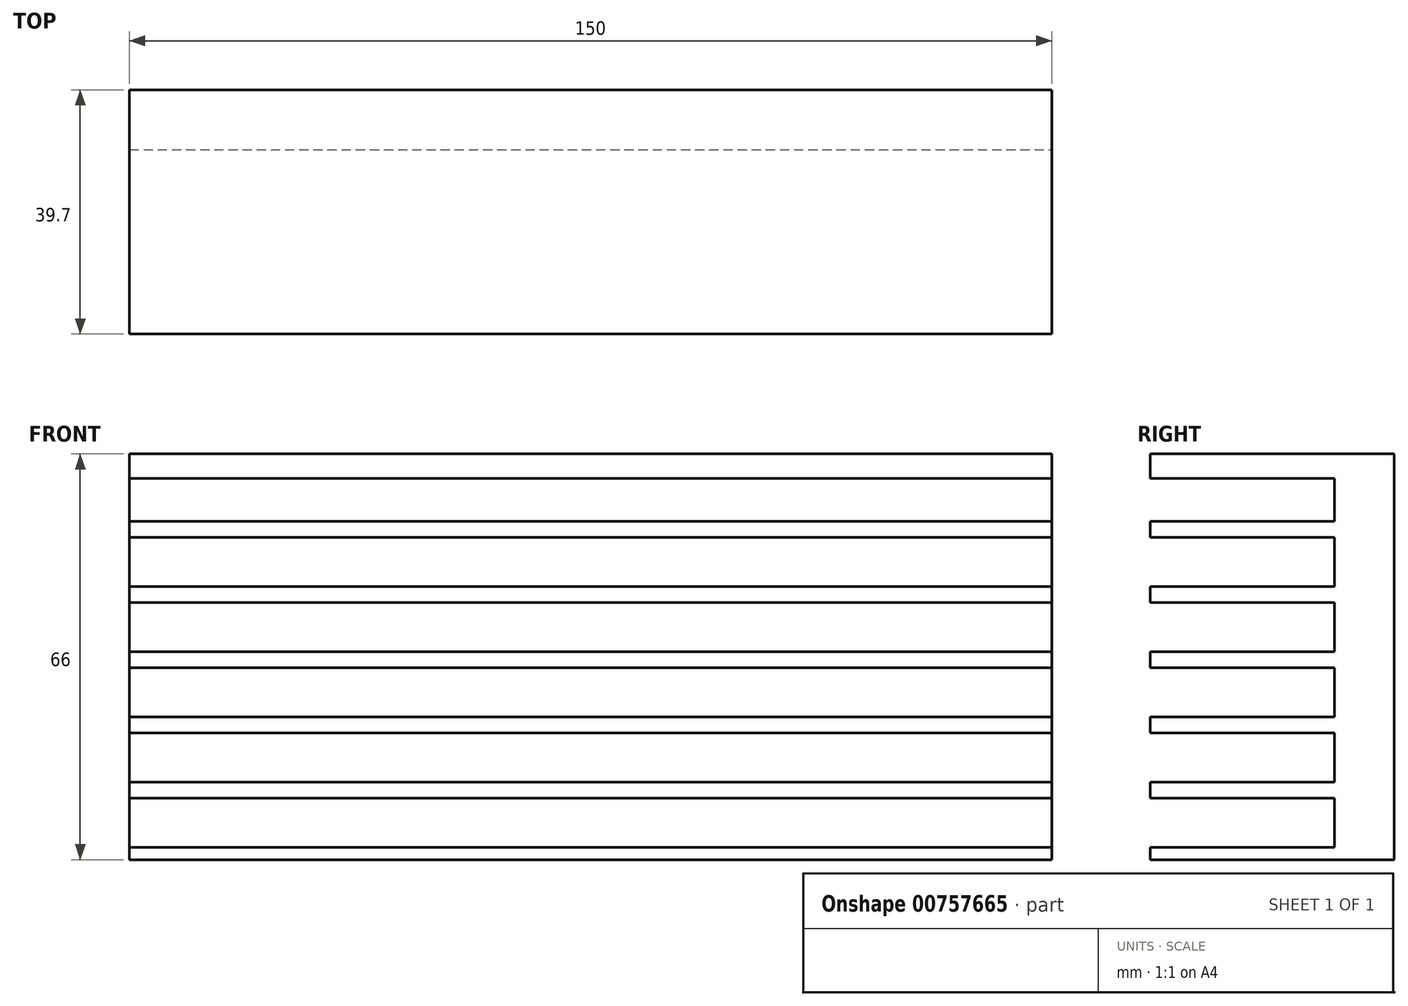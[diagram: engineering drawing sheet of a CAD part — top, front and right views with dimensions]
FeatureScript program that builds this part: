
annotation { "Feature Type Name" : "Feature", "Feature Type Description" : "" }
export const myFeature = defineFeature(function(context is Context, id is Id, definition is map)
    precondition{}
    {
        {
            var Q0;
            Q0=qCreatedBy(makeId("Front.planeOp"),FACE);
            var sketch = newSketch(context, id + "F0", { "sketchPlane" : qUnion([Q0])});
            skLineSegment(sketch, "E0.bottom", {"start": v(-143.7, 34.15) * mm, "end": v(6.3, 34.15) * mm});
            skLineSegment(sketch, "E0.top", {"start": v(-143.7, -31.85) * mm, "end": v(6.3, -31.85) * mm});
            skLineSegment(sketch, "E0.left", {"start": v(-143.7, 34.15) * mm, "end": v(-143.7, -31.85) * mm});
            skLineSegment(sketch, "E0.right", {"start": v(6.3, 34.15) * mm, "end": v(6.3, -31.85) * mm});
            skSolve(sketch);
        }
        {
            var Q0;
            Q0 = qSketchRegion(id + "F0", true);
            var Q1;
            Q1=makeQuery(id+"F0.imprint","IMPRINT",FACE,{"disambiguationData":[TD([[makeQuery(id+"F0.imprint","IMPRINT",EDGE,{"derivedFrom":sQuery(id+"F0.wireOp",EDGE,"E0.bottom")}),-1.0]])]});
            extrude(context, id + "F1", {"entities" : qUnion([Q0, Q1]), "depth" : 39.7 * mm, "offsetDistance" : 25 * mm});
        }
        {
            var Q0;
            Q0=makeQuery(id+"F1.opExtrude","CAP_FACE",FACE,{"disambiguationData":[OSD([sQuery(id+"F0.wireOp",EDGE,"E0.bottom"),sQuery(id+"F0.wireOp",EDGE,"E0.top"),sQuery(id+"F0.wireOp",EDGE,"E0.left"),sQuery(id+"F0.wireOp",EDGE,"E0.right")])],"isStart":false});
            var sketch = newSketch(context, id + "F2", { "sketchPlane" : qUnion([Q0])});
            skLineSegment(sketch, "E1", {"start": v(-143.7, 30.15) * mm, "end": v(6.3, 30.15) * mm});
            skLineSegment(sketch, "E2", {"start": v(-143.7, 20.55) * mm, "end": v(6.3, 20.55) * mm});
            skLineSegment(sketch, "E3", {"start": v(-143.7, 23.15) * mm, "end": v(6.3, 23.15) * mm});
            skLineSegment(sketch, "E4", {"start": v(-143.7, 12.55) * mm, "end": v(6.3, 12.55) * mm});
            skLineSegment(sketch, "E5", {"start": v(-143.7, 9.95) * mm, "end": v(6.3, 9.95) * mm});
            skLineSegment(sketch, "E6", {"start": v(-143.7, 1.95) * mm, "end": v(6.3, 1.95) * mm});
            skLineSegment(sketch, "E7", {"start": v(-143.7, -0.65) * mm, "end": v(6.3, -0.65) * mm});
            skLineSegment(sketch, "E8", {"start": v(-143.7, -8.65) * mm, "end": v(6.3, -8.65) * mm});
            skLineSegment(sketch, "E9", {"start": v(-143.7, -11.25) * mm, "end": v(6.3, -11.25) * mm});
            skLineSegment(sketch, "E10", {"start": v(-143.7, -19.25) * mm, "end": v(6.3, -19.25) * mm});
            skLineSegment(sketch, "E11", {"start": v(-143.7, -21.85) * mm, "end": v(6.3, -21.85) * mm});
            skLineSegment(sketch, "E12", {"start": v(-143.7, -29.85) * mm, "end": v(6.3, -29.85) * mm});
            skSolve(sketch);
        }
        {
            var Q0;
            Q0 = qSketchRegion(id + "F2", true);
            var Q1;
            {var subQ0=sQuery(id+"F2.wireOp",EDGE,"E1");Q1=makeQuery(id+"F2.imprint","IMPRINT",FACE,{"disambiguationData":[TD([[makeQuery(id+"F2.imprint","IMPRINT",EDGE,{"derivedFrom":subQ0}),-1.0]])]});}
            extrude(context, id + "F3", {"entities" : qUnion([Q0, Q1]), "operationType" : NewBodyOperationType.REMOVE, "oppositeDirection" : true, "depth" : 30 * mm, "offsetDistance" : 25 * mm});
        }
        {
            var Q0;
            {var subQ0=sQuery(id+"F2.wireOp",EDGE,"E2");Q0=makeQuery(id+"F2.imprint","IMPRINT",FACE,{"disambiguationData":[TD([[makeQuery(id+"F2.imprint","IMPRINT",EDGE,{"derivedFrom":subQ0}),-1.0]])]});}
            extrude(context, id + "F4", {"entities" : qUnion([Q0]), "operationType" : NewBodyOperationType.REMOVE, "oppositeDirection" : true, "depth" : 30 * mm, "offsetDistance" : 25 * mm});
        }
        {
            var Q0;
            Q0 = qSketchRegion(id + "F2", true);
            var Q1;
            {var subQ0=sQuery(id+"F2.wireOp",EDGE,"E5");Q1=makeQuery(id+"F2.imprint","IMPRINT",FACE,{"disambiguationData":[TD([[makeQuery(id+"F2.imprint","IMPRINT",EDGE,{"derivedFrom":subQ0}),-1.0]])]});}
            extrude(context, id + "F5", {"entities" : qUnion([Q0, Q1]), "operationType" : NewBodyOperationType.REMOVE, "oppositeDirection" : true, "depth" : 30 * mm, "offsetDistance" : 25 * mm});
        }
        {
            var Q0;
            Q0 = qSketchRegion(id + "F2", true);
            var Q1;
            {var subQ0=sQuery(id+"F2.wireOp",EDGE,"E7");Q1=makeQuery(id+"F2.imprint","IMPRINT",FACE,{"disambiguationData":[TD([[makeQuery(id+"F2.imprint","IMPRINT",EDGE,{"derivedFrom":subQ0}),-1.0]])]});}
            extrude(context, id + "F6", {"entities" : qUnion([Q0, Q1]), "operationType" : NewBodyOperationType.REMOVE, "oppositeDirection" : true, "depth" : 30 * mm, "offsetDistance" : 25 * mm});
        }
        {
            var Q0;
            {var subQ0=sQuery(id+"F2.wireOp",EDGE,"E9");Q0=makeQuery(id+"F2.imprint","IMPRINT",FACE,{"disambiguationData":[TD([[makeQuery(id+"F2.imprint","IMPRINT",EDGE,{"derivedFrom":subQ0}),-1.0]])]});}
            extrude(context, id + "F7", {"entities" : qUnion([Q0]), "operationType" : NewBodyOperationType.REMOVE, "oppositeDirection" : true, "depth" : 30 * mm, "offsetDistance" : 25 * mm});
        }
        {
            var Q0;
            {var subQ0=sQuery(id+"F2.wireOp",EDGE,"E11");Q0=makeQuery(id+"F2.imprint","IMPRINT",FACE,{"disambiguationData":[TD([[makeQuery(id+"F2.imprint","IMPRINT",EDGE,{"derivedFrom":subQ0}),-1.0]])]});}
            extrude(context, id + "F8", {"entities" : qUnion([Q0]), "operationType" : NewBodyOperationType.REMOVE, "oppositeDirection" : true, "depth" : 30 * mm, "offsetDistance" : 25 * mm});
        }
    });
